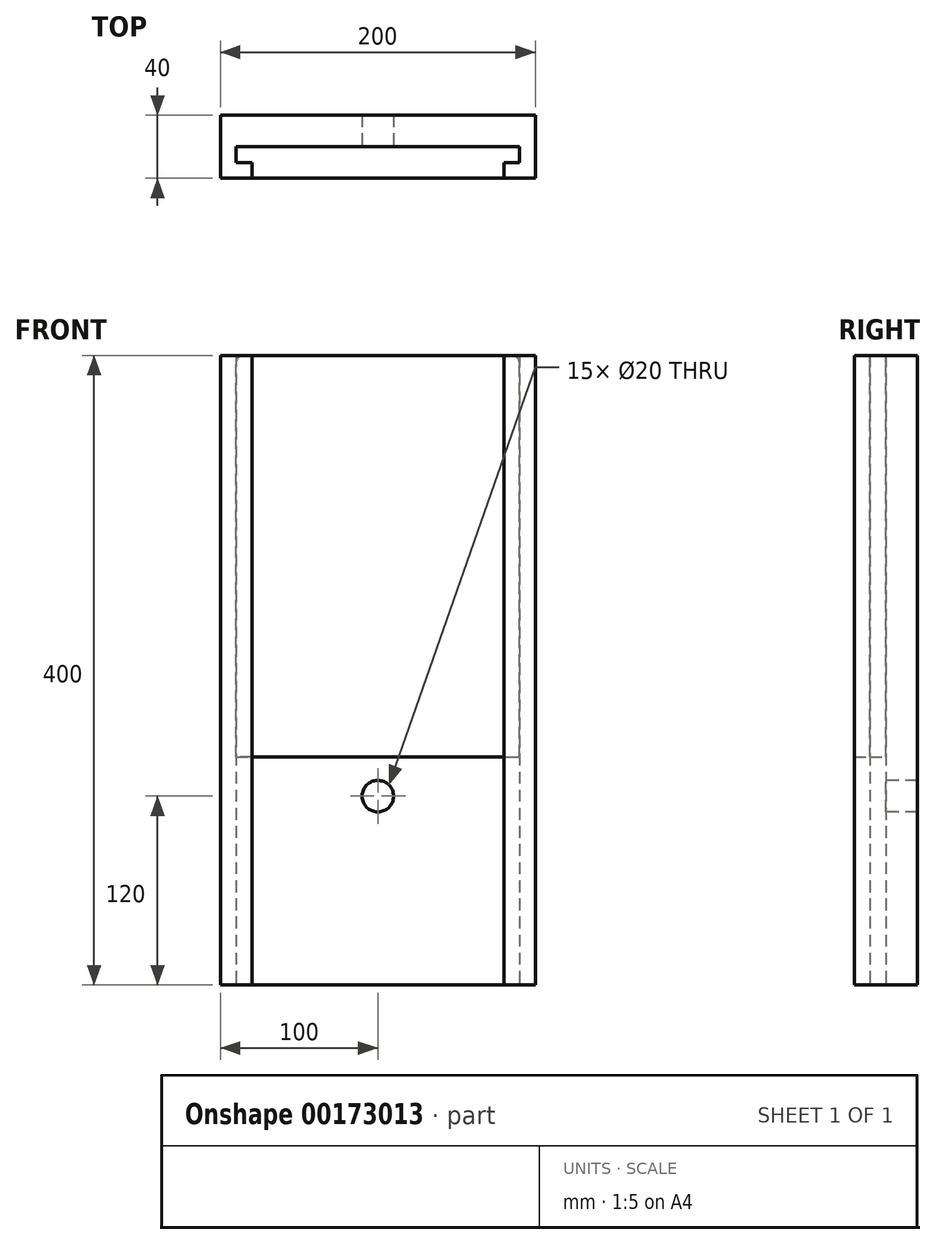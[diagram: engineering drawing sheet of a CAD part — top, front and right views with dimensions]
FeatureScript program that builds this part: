
annotation { "Feature Type Name" : "Feature", "Feature Type Description" : "" }
export const myFeature = defineFeature(function(context is Context, id is Id, definition is map)
    precondition{}
    {
        {
            var Q0;
            Q0=qCreatedBy(makeId("Top.planeOp"),FACE);
            var sketch = newSketch(context, id + "F0", { "sketchPlane" : qUnion([Q0])});
            skLineSegment(sketch, "E0", {"start": v(0, 40) * mm, "end": v(100, 40) * mm});
            skLineSegment(sketch, "E1", {"start": v(100, 40) * mm, "end": v(100, 0) * mm});
            skLineSegment(sketch, "E2", {"start": v(100, 0) * mm, "end": v(80, 0) * mm});
            skLineSegment(sketch, "E3", {"start": v(80, 0) * mm, "end": v(80, 10) * mm});
            skLineSegment(sketch, "E4", {"start": v(80, 10) * mm, "end": v(90, 10) * mm});
            skLineSegment(sketch, "E5", {"start": v(90, 10) * mm, "end": v(90, 20) * mm});
            skLineSegment(sketch, "E6", {"start": v(90, 20) * mm, "end": v(0, 20) * mm});
            skLineSegment(sketch, "E7", {"start": v(0, 40) * mm, "end": v(0, 0) * mm, "construction": true});
            skLineSegment(sketch, "E8.MirrorCS", {"start": v(0, 40) * mm, "end": v(-100, 40) * mm});
            skLineSegment(sketch, "E9.MirrorCS", {"start": v(-100, 40) * mm, "end": v(-100, 0) * mm});
            skLineSegment(sketch, "E10.MirrorCS", {"start": v(-100, 0) * mm, "end": v(-80, 0) * mm});
            skLineSegment(sketch, "E11.MirrorCS", {"start": v(-80, 0) * mm, "end": v(-80, 10) * mm});
            skLineSegment(sketch, "E12.MirrorCS", {"start": v(-80, 10) * mm, "end": v(-90, 10) * mm});
            skLineSegment(sketch, "E13.MirrorCS", {"start": v(-90, 10) * mm, "end": v(-90, 20) * mm});
            skLineSegment(sketch, "E14.MirrorCS", {"start": v(-90, 20) * mm, "end": v(0, 20) * mm});
            skSolve(sketch);
        }
        {
            var Q0;
            Q0=qSketchRegion(id+"F0",true);
            extrude(context, id + "F1", {"entities" : qUnion([Q0]), "depth" : 280 * mm, "hasSecondDirection" : true, "secondDirectionOppositeDirection" : true, "secondDirectionDepth" : 120 * mm});
        }
        {
            var Q0;
            Q0=makeQuery(id+"F1.opExtrude","SWEPT_FACE",FACE,{"disambiguationData":[OSD([sQuery(id+"F0.wireOp",EDGE,"E6"),sQuery(id+"F0.wireOp",EDGE,"E14.MirrorCS")])]});
            var sketch = newSketch(context, id + "F2", { "sketchPlane" : qUnion([Q0])});
            skCircle(sketch, "E15", {"center": v(0, 0) * mm, "radius": 10 * mm});
            skSolve(sketch);
        }
        {
            var Q0;
            Q0=qSketchRegion(id+"F2",true);
            extrude(context, id + "F3", {"entities" : qUnion([Q0]), "operationType" : NewBodyOperationType.REMOVE, "oppositeDirection" : true, "depth" : 20 * mm});
        }
        {
            var Q0;
            Q0=makeQuery(id+"F1.opExtrude","CAP_FACE",FACE,{"disambiguationData":[OSD([sQuery(id+"F0.wireOp",EDGE,"E0"),sQuery(id+"F0.wireOp",EDGE,"E1"),sQuery(id+"F0.wireOp",EDGE,"E2"),sQuery(id+"F0.wireOp",EDGE,"E3"),sQuery(id+"F0.wireOp",EDGE,"E4"),sQuery(id+"F0.wireOp",EDGE,"E5"),sQuery(id+"F0.wireOp",EDGE,"E6"),sQuery(id+"F0.wireOp",EDGE,"E8.MirrorCS"),sQuery(id+"F0.wireOp",EDGE,"E9.MirrorCS"),sQuery(id+"F0.wireOp",EDGE,"E10.MirrorCS"),sQuery(id+"F0.wireOp",EDGE,"E11.MirrorCS"),sQuery(id+"F0.wireOp",EDGE,"E12.MirrorCS"),sQuery(id+"F0.wireOp",EDGE,"E13.MirrorCS"),sQuery(id+"F0.wireOp",EDGE,"E14.MirrorCS")])],"isStart":false});
            var sketch = newSketch(context, id + "F4", { "sketchPlane" : qUnion([Q0])});
            skLineSegment(sketch, "E16", {"start": v(-90, 20) * mm, "end": v(-90, 10) * mm});
            skLineSegment(sketch, "E17", {"start": v(-90, 10) * mm, "end": v(-80, 10) * mm});
            skLineSegment(sketch, "E18", {"start": v(-80, 10) * mm, "end": v(-80, 0) * mm});
            skLineSegment(sketch, "E19", {"start": v(-80, 0) * mm, "end": v(80, 0) * mm});
            skLineSegment(sketch, "E20", {"start": v(80, 0) * mm, "end": v(80, 10) * mm});
            skLineSegment(sketch, "E21", {"start": v(80, 10) * mm, "end": v(90, 10) * mm});
            skLineSegment(sketch, "E22", {"start": v(90, 10) * mm, "end": v(90, 20) * mm});
            skLineSegment(sketch, "E23", {"start": v(90, 20) * mm, "end": v(-90, 20) * mm});
            skSolve(sketch);
        }
        {
            var Q0;
            Q0=qSketchRegion(id+"F4",true);
            extrude(context, id + "F5", {"entities" : qUnion([Q0]), "oppositeDirection" : true, "depth" : 255 * mm});
        }
        {
            var Q0;
            Q0=makeQuery(id+"F5.opExtrude","CAP_EDGE",EDGE,{"disambiguationData":[OSD([sQuery(id+"F4.wireOp",EDGE,"E16")])],"isStart":true});
            fillet(context, id + "F6", {"entities" : qUnion([Q0]), "radius" : 5 * mm, "tangentPropagation" : true, "allowEdgeOverflow" : false});
        }
        {
            var Q0;
            Q0=makeQuery(id+"F5.opExtrude","CAP_EDGE",EDGE,{"disambiguationData":[OSD([sQuery(id+"F4.wireOp",EDGE,"E22")])],"isStart":true});
            fillet(context, id + "F7", {"entities" : qUnion([Q0]), "radius" : 5 * mm, "tangentPropagation" : true, "allowEdgeOverflow" : false});
        }
    });
